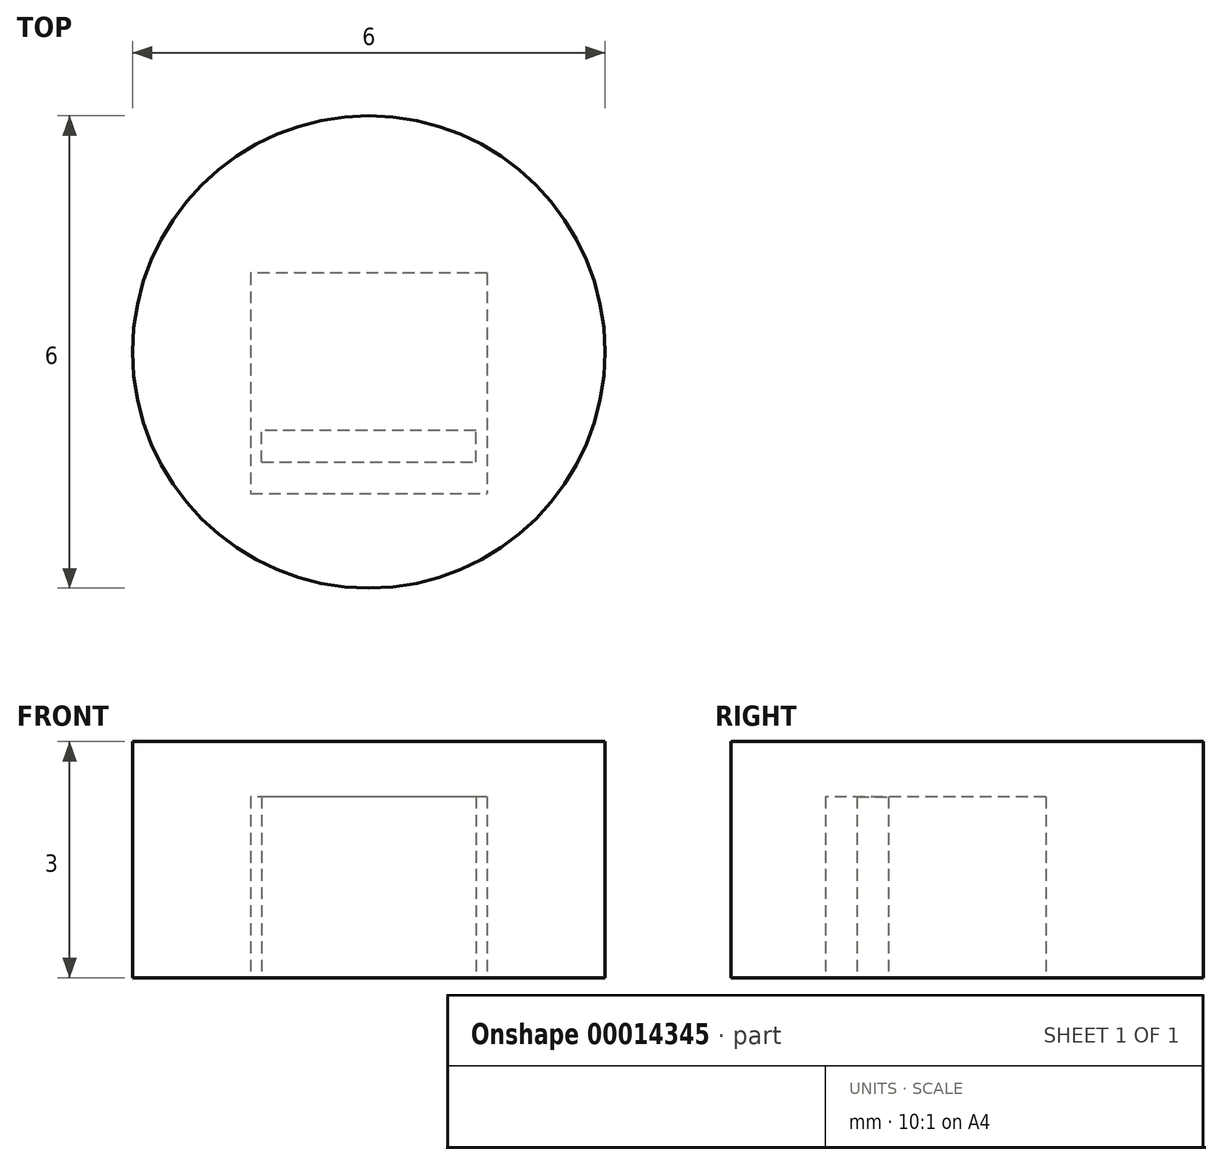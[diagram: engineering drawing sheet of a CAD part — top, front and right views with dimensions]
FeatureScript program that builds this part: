
annotation { "Feature Type Name" : "Feature", "Feature Type Description" : "" }
export const myFeature = defineFeature(function(context is Context, id is Id, definition is map)
    precondition{}
    {
        {
            var Q0;
            Q0=qCreatedBy(makeId("Top.planeOp"),FACE);
            var sketch = newSketch(context, id + "F0", { "sketchPlane" : qUnion([Q0])});
            skCircle(sketch, "E0", {"center": v(0, 0) * mm, "radius": 3 * mm});
            skLineSegment(sketch, "E1.rect.bottom", {"start": v(1.5, -1) * mm, "end": v(-1.5, -1) * mm});
            skLineSegment(sketch, "E1.rect.top", {"start": v(1.5, 1) * mm, "end": v(-1.5, 1) * mm});
            skLineSegment(sketch, "E1.rect.left", {"start": v(1.5, -1) * mm, "end": v(1.5, 1) * mm});
            skLineSegment(sketch, "E1.rect.right", {"start": v(-1.5, -1) * mm, "end": v(-1.5, 1) * mm});
            skLineSegment(sketch, "E2.bottom", {"start": v(-1.5, -1) * mm, "end": v(1.5, -1) * mm});
            skLineSegment(sketch, "E2.top", {"start": v(-1.5, -1.8) * mm, "end": v(1.5, -1.8) * mm});
            skLineSegment(sketch, "E2.left", {"start": v(-1.5, -1) * mm, "end": v(-1.5, -1.8) * mm});
            skLineSegment(sketch, "E2.right", {"start": v(1.5, -1) * mm, "end": v(1.5, -1.8) * mm});
            skLineSegment(sketch, "E3.top", {"start": v(-1.5, -1.4) * mm, "end": v(1.5, -1.4) * mm});
            skLineSegment(sketch, "E3.left", {"start": v(-1.5, -1.8) * mm, "end": v(-1.5, -1.4) * mm});
            skLineSegment(sketch, "E3.right", {"start": v(1.5, -1.8) * mm, "end": v(1.5, -1.4) * mm});
            skLineSegment(sketch, "E4", {"start": v(0, -1) * mm, "end": v(0, -1.4) * mm, "construction": true});
            skLineSegment(sketch, "E5.rect.bottom", {"start": v(1.36, -1.4) * mm, "end": v(-1.36, -1.4) * mm, "construction": true});
            skLineSegment(sketch, "E5.rect.top", {"start": v(1.36, -1) * mm, "end": v(-1.36, -1) * mm, "construction": true});
            skLineSegment(sketch, "E5.rect.left", {"start": v(1.36, -1.4) * mm, "end": v(1.36, -1) * mm});
            skLineSegment(sketch, "E5.rect.right", {"start": v(-1.36, -1.4) * mm, "end": v(-1.36, -1) * mm});
            skPoint(sketch, "E5.rect.middle", {"position": v(0, -1.2) * mm});
            skSolve(sketch);
        }
        {
            var Q0;
            Q0=makeQuery(id+"F0.imprint","IMPRINT",FACE,{"disambiguationData":[TD([[makeQuery(id+"F0.imprint","IMPRINT",EDGE,{"derivedFrom":sQuery(id+"F0.wireOp",EDGE,"E0")}),1.0]])]});
            extrude(context, id + "F1", {"entities" : qUnion([Q0]), "depth" : 3 * mm});
        }
        {
            var Q0;
            Q0=makeQuery(id+"F0.imprint","IMPRINT",FACE,{"disambiguationData":[TD([[makeQuery(id+"F0.imprint","IMPRINT",EDGE,{"derivedFrom":sQuery(id+"F0.wireOp",EDGE,"E2.top")}),1.0]])]});
            extrude(context, id + "F2", {"entities" : qUnion([Q0]), "operationType" : NewBodyOperationType.ADD, "depth" : 3 * mm, "hasSecondDirection" : true, "secondDirectionOppositeDirection" : false, "secondDirectionDepth" : 2.3 * mm});
        }
        {
            var Q0;
            {var subQ1=sQuery(id+"F0.wireOp",EDGE,"E5.rect.left");Q0=makeQuery(id+"F0.imprint","IMPRINT",FACE,{"disambiguationData":[TD([[makeQuery(id+"F0.imprint","IMPRINT",EDGE,{"derivedFrom":subQ1}),1.0]])]});}
            extrude(context, id + "F3", {"entities" : qUnion([Q0]), "operationType" : NewBodyOperationType.ADD, "depth" : 3 * mm});
        }
        {
            var Q0;
            Q0=qCreatedBy(makeId("Right.planeOp"),FACE);
            var sketch = newSketch(context, id + "F4", { "sketchPlane" : qUnion([Q0])});
            skCircle(sketch, "E6", {"center": v(0, 1) * mm, "radius": 1 * mm});
            skLineSegment(sketch, "E7", {"start": v(1, 1) * mm, "end": v(1, 0) * mm});
            skLineSegment(sketch, "E8", {"start": v(1, 0) * mm, "end": v(0, 0) * mm});
            skSolve(sketch);
        }
        {
            var Q0;
            Q0 = qSketchRegion(id + "F4", true);
            extrude(context, id + "F5", {"entities" : qUnion([Q0]), "operationType" : NewBodyOperationType.REMOVE, "oppositeDirection" : true, "depth" : 1.5 * mm, "hasSecondDirection" : true, "secondDirectionOppositeDirection" : false, "secondDirectionDepth" : 1.5 * mm});
        }
        {
            var Q0;
            Q0=makeQuery(id+"F0.imprint","IMPRINT",FACE,{"disambiguationData":[TD([[makeQuery(id+"F0.imprint","IMPRINT",EDGE,{"derivedFrom":sQuery(id+"F0.wireOp",EDGE,"E1.rect.top")}),1.0]])]});
            var Q1;
            {var subQ2=sQuery(id+"F0.wireOp",EDGE,"E2.left");Q1=makeQuery(id+"F0.imprint","IMPRINT",FACE,{"disambiguationData":[TD([[makeQuery(id+"F0.imprint","IMPRINT",EDGE,{"derivedFrom":subQ2}),1.0]])]});}
            var Q2;
            {var subQ2=sQuery(id+"F0.wireOp",EDGE,"E2.right");Q2=makeQuery(id+"F0.imprint","IMPRINT",FACE,{"disambiguationData":[TD([[makeQuery(id+"F0.imprint","IMPRINT",EDGE,{"derivedFrom":subQ2}),-1.0]])]});}
            extrude(context, id + "F6", {"entities" : qUnion([Q0, Q1, Q2]), "operationType" : NewBodyOperationType.ADD, "depth" : 3 * mm, "hasSecondDirection" : true, "secondDirectionOppositeDirection" : false, "secondDirectionDepth" : 2.3 * mm});
        }
    });
